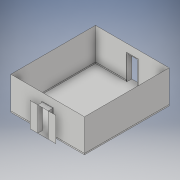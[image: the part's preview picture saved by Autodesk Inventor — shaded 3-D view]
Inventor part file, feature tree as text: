
AUTODESK INVENTOR PART (.ipt)
format: ipt  version: 2017 (Build 210142000, 142)  size: 243,200 bytes
history: native  units: in
note: dims shown in document units (in); Inventor stores cm internally (conversion verified against a paired STEP export)
features: extrude x6, mirror x4, sketch x4, shell x1, other x1
ambient origin geometry x8: Origin, YZ Plane, XZ Plane, XY Plane, X Axis, Y Axis, Z Axis, Center Point
bodies: Solid1 (feature_tree), Solid2 (feature_tree)
feature tree (16):
  extrude  "main body"  Depth=22.0in
  shell  "hollow interior"  Thickness=11.0in
  extrude  "door frame"  Depth=1.0in
  extrude  "Extrusion5"  Depth=2.875in
  extrude  "door trim"  Depth=0.0417in
  extrude  "top of door trim"  Depth=0.1667in
  mirror  "mirror plane for door trim"
  mirror  "Mirror door trim"
  mirror  "mirror plane for door"
  mirror  "Mirror2"
  extrude  "floor trim"  Depth=1.0in TaperAngle=0.0deg
  other  "remove outer edges"
  sketch  "Sketch1"  dims[d0=25.0in d1=22.0in d2=11.0in d3=0.0in]
  sketch  "Sketch3"  dims[d4=1.0in d5=1.4375in]
  sketch  "Sketch4"  dims[d6=6.6667in d7=2.875in]
  sketch  "Sketch5"  dims[d8=1.0in d9=0.0in d10=0.0417in d11=0.1667in d12=1.0in d13=0.0in d14=0.1667in d15=1.0in d16=0.0in d17=7.0in d18=6.6667in d19=0.5in d20=0.0in d21=0.0104in d22=0.0104in d23=0.3438in d24=0.0in d25=0.0104in d26=0.0104in]
